FCSTD DOCUMENT  (FreeCAD 0.20R0.20.2)
Label: 003
License: All rights reserved
LicenseURL: http://en.wikipedia.org/wiki/All_rights_reserved
objects: Sketcher::SketchObject×1
note: 1 computed .brp shape members not serialized (recipe doc carries the construction recipe); baked Part::Feature solids carry a one-line shape summary decoded from their .brp

FEATURE [Sketcher::SketchObject] Sketch
  FullyConstrained = false
  sketch-geometry (18):
    g0: Circle CenterX=7 CenterY=0 CenterZ=0 NormalX=0 NormalY=0 NormalZ=1 AngleXU=0 Radius=2
    g1: Circle CenterX=0 CenterY=7 CenterZ=0 NormalX=0 NormalY=0 NormalZ=1 AngleXU=0 Radius=2
    g2: Circle CenterX=0 CenterY=0 CenterZ=0 NormalX=0 NormalY=0 NormalZ=1 AngleXU=0 Radius=2.8
    g3: Circle CenterX=-7 CenterY=0 CenterZ=0 NormalX=0 NormalY=0 NormalZ=1 AngleXU=0 Radius=2
    g4: Circle CenterX=0 CenterY=-7 CenterZ=0 NormalX=0 NormalY=0 NormalZ=1 AngleXU=0 Radius=2
    g5: LineSegment StartX=-18.75 StartY=-10.5 StartZ=0 EndX=18.75 EndY=-10.5 EndZ=0
    g6: LineSegment StartX=18.75 StartY=10.5 StartZ=0 EndX=18.75 EndY=-10.5 EndZ=0
    g7: LineSegment StartX=-18.75 StartY=10.5 StartZ=0 EndX=-18.75 EndY=-10.5 EndZ=0
    g8: LineSegment StartX=-16.55 StartY=8.3 StartZ=0 EndX=-3.5 EndY=8.3 EndZ=0
    g9: LineSegment StartX=-3.5 StartY=8.3 StartZ=0 EndX=-3.5 EndY=3.5 EndZ=0
    g10: LineSegment StartX=-3.5 StartY=3.5 StartZ=0 EndX=-16.55 EndY=3.5 EndZ=0
    g11: LineSegment StartX=-16.55 StartY=3.5 StartZ=0 EndX=-16.55 EndY=8.3 EndZ=0
    g12: LineSegment StartX=-18.75 StartY=10.5 StartZ=0 EndX=-18.75 EndY=14.0694 EndZ=0
    g13: LineSegment StartX=-18.75 StartY=14.0694 StartZ=0 EndX=-21.5732 EndY=14.0694 EndZ=0
    g14: LineSegment StartX=-18.75 StartY=10.5 StartZ=0 EndX=-16.55 EndY=10.5 EndZ=0
    g15: LineSegment StartX=-16.55 StartY=10.5 StartZ=0 EndX=-16.55 EndY=8.3 EndZ=0
    g16: LineSegment StartX=0 StartY=7 StartZ=0 EndX=-3.5 EndY=7 EndZ=0
    g17: LineSegment StartX=-7 StartY=0 StartZ=0 EndX=-7 EndY=3.5 EndZ=0
  constraints (40):
    c: Block(g2)
    c: Block(g1)
    c: Block(g0)
    c: Block(g3)
    c: Block(g4)
    c: Horizontal(g5)
    c: Block(g5)
    c: Coincident(g6,g5)
    c: Vertical(g6)
    c: Coincident(g7,g5)
    c: Vertical(g7)
    c: Coincident(g8,g9)
    c: Coincident(g9,g10)
    c: Coincident(g10,g11)
    c: Coincident(g11,g8)
    c: Horizontal(g8)
    c: Horizontal(g10)
    c: Vertical(g9)
    c: Vertical(g11)
    c: Vertical(g12)
    c: Block(g12)
    c: Coincident(g13,g12)
    c: Horizontal(g13)
    c: Block(g13)
    c: Coincident(g14,g7)
    c: Horizontal(g14)
    c: Distance(g14) = 2.2
    c: Block(g7)
    c: Coincident(g15,g14)
    c: Vertical(g15)
    c: Distance(g15) = 2.2
    c: Coincident(g8,g15)
    c: Coincident(g16,g1)
    c: PointOnObject(g16,g9)
    c: Horizontal(g16)
    c: Distance(g16) = 3.5
    c: Coincident(g17,g3)
    c: PointOnObject(g17,g10)
    c: Vertical(g17)
    c: Distance(g17) = 3.5
